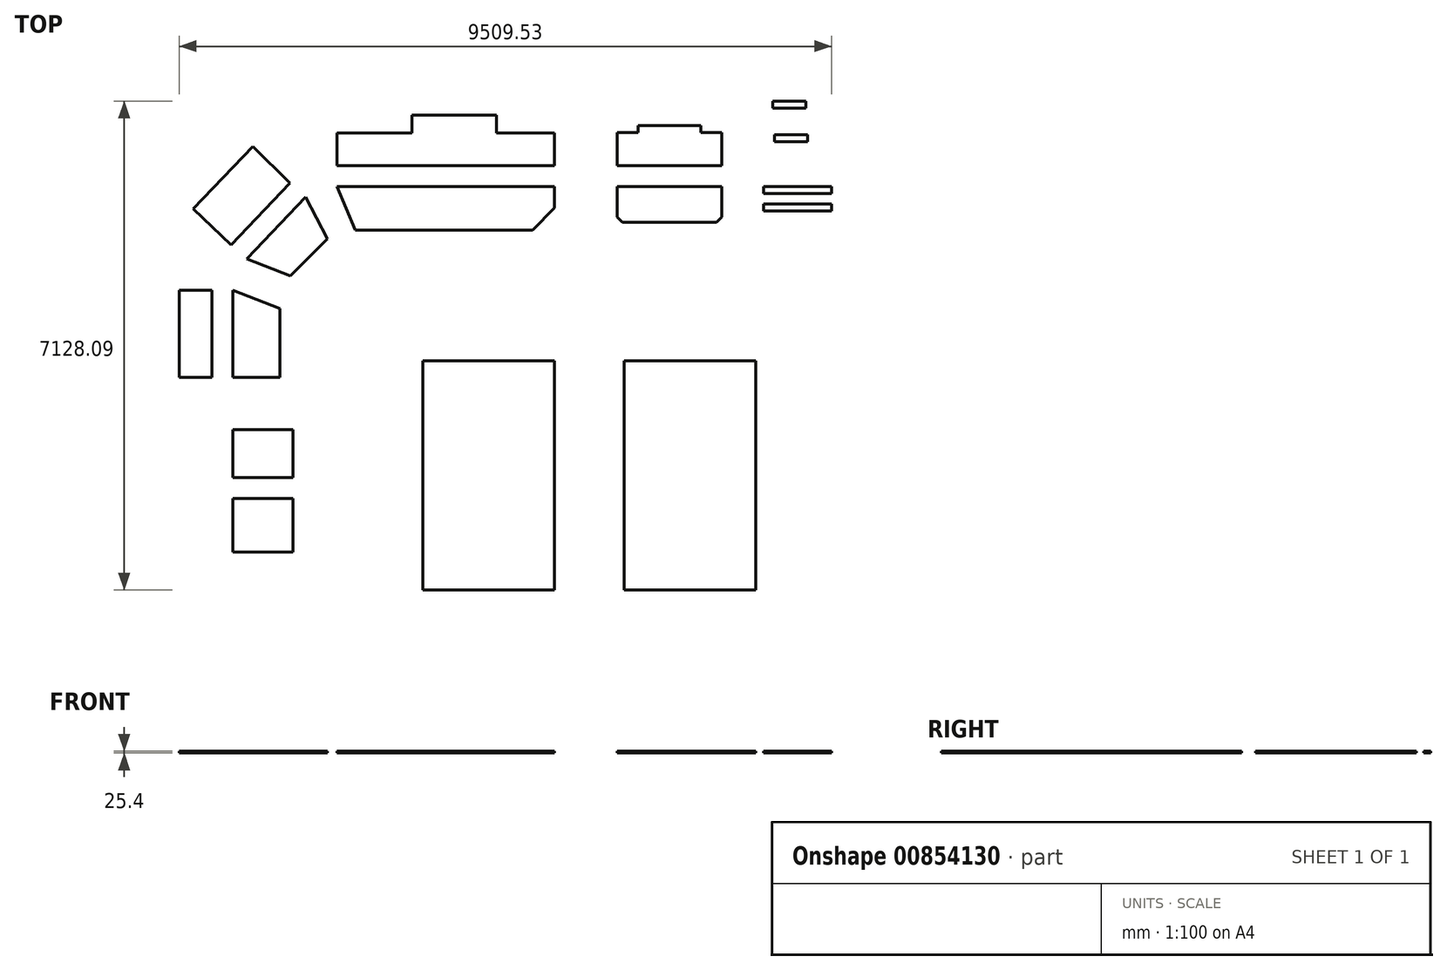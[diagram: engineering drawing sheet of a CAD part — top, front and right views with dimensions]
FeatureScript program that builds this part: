
annotation { "Feature Type Name" : "Feature", "Feature Type Description" : "" }
export const myFeature = defineFeature(function(context is Context, id is Id, definition is map)
    precondition{}
    {
        {
            var Q0;
            Q0=qCreatedBy(makeId("Top.planeOp"),FACE);
            var sketch = newSketch(context, id + "F0", { "sketchPlane" : qUnion([Q0])});
            skLineSegment(sketch, "E0", {"start": v(-3168.65, 0) * mm, "end": v(-2906.4, -633.1) * mm});
            skLineSegment(sketch, "E1", {"start": v(-2906.4, -633.1) * mm, "end": v(-321.96, -633.1) * mm});
            skLineSegment(sketch, "E2", {"start": v(-321.96, -633.1) * mm, "end": v(0, -311.15) * mm});
            skLineSegment(sketch, "E3", {"start": v(0, -311.15) * mm, "end": v(0, 0) * mm});
            skLineSegment(sketch, "E4", {"start": v(0, 0) * mm, "end": v(-3168.65, 0) * mm});
            skLineSegment(sketch, "E5", {"start": v(-3168.65, 781.05) * mm, "end": v(-3168.65, 304.8) * mm});
            skLineSegment(sketch, "E6", {"start": v(-3168.65, 304.8) * mm, "end": v(0, 304.8) * mm});
            skLineSegment(sketch, "E7", {"start": v(0, 304.8) * mm, "end": v(0, 781.05) * mm});
            skLineSegment(sketch, "E8", {"start": v(0, 781.05) * mm, "end": v(-847.73, 781.05) * mm});
            skLineSegment(sketch, "E9", {"start": v(-847.73, 781.05) * mm, "end": v(-847.73, 1041.4) * mm});
            skLineSegment(sketch, "E10", {"start": v(-847.73, 1041.4) * mm, "end": v(-2076.45, 1041.4) * mm});
            skLineSegment(sketch, "E11", {"start": v(-2076.45, 1041.4) * mm, "end": v(-2076.45, 781.05) * mm});
            skLineSegment(sketch, "E12", {"start": v(-2076.45, 781.05) * mm, "end": v(-3168.65, 781.05) * mm});
            skLineSegment(sketch, "E13", {"start": v(-3309.69, -760.97) * mm, "end": v(-3848.5, -1299.79) * mm});
            skLineSegment(sketch, "E14", {"start": v(-3848.5, -1299.79) * mm, "end": v(-4487.42, -1050.58) * mm});
            skLineSegment(sketch, "E15", {"start": v(-4487.42, -1050.58) * mm, "end": v(-3625.85, -152.4) * mm});
            skLineSegment(sketch, "E16", {"start": v(-3625.85, -152.4) * mm, "end": v(-3309.69, -760.97) * mm});
            skLineSegment(sketch, "E17", {"start": v(-3854.45, 49.2) * mm, "end": v(-4716.02, -848.97) * mm});
            skLineSegment(sketch, "E18", {"start": v(-4716.02, -848.97) * mm, "end": v(-5268.08, -323.81) * mm});
            skLineSegment(sketch, "E19", {"start": v(-5268.08, -323.81) * mm, "end": v(-4397.72, 583.53) * mm});
            skLineSegment(sketch, "E20", {"start": v(-4397.72, 583.53) * mm, "end": v(-3854.45, 49.2) * mm});
            skLineSegment(sketch, "E21", {"start": v(-4686.7, -1507.78) * mm, "end": v(-4000.9, -1774.48) * mm});
            skLineSegment(sketch, "E22", {"start": v(-4000.9, -1774.48) * mm, "end": v(-4000.9, -2777.78) * mm});
            skLineSegment(sketch, "E23", {"start": v(-4000.9, -2777.78) * mm, "end": v(-4686.7, -2777.78) * mm});
            skLineSegment(sketch, "E24", {"start": v(-4686.7, -2777.78) * mm, "end": v(-4686.7, -1507.78) * mm});
            skLineSegment(sketch, "E25.bottom", {"start": v(-5470.93, -1507.78) * mm, "end": v(-4991.5, -1507.78) * mm});
            skLineSegment(sketch, "E25.top", {"start": v(-5470.93, -2777.78) * mm, "end": v(-4991.5, -2777.78) * mm});
            skLineSegment(sketch, "E25.left", {"start": v(-5470.93, -1507.78) * mm, "end": v(-5470.93, -2777.78) * mm});
            skLineSegment(sketch, "E25.right", {"start": v(-4991.5, -1507.78) * mm, "end": v(-4991.5, -2777.78) * mm});
            skLineSegment(sketch, "E26", {"start": v(914.4, 787.4) * mm, "end": v(914.4, 304.8) * mm});
            skLineSegment(sketch, "E27", {"start": v(914.4, 304.8) * mm, "end": v(2438.4, 304.8) * mm});
            skLineSegment(sketch, "E28", {"start": v(2438.4, 304.8) * mm, "end": v(2438.4, 787.4) * mm});
            skLineSegment(sketch, "E29", {"start": v(2438.4, 787.4) * mm, "end": v(2133.6, 787.4) * mm});
            skLineSegment(sketch, "E30", {"start": v(2133.6, 787.4) * mm, "end": v(2133.6, 892.17) * mm});
            skLineSegment(sketch, "E31", {"start": v(2133.6, 892.17) * mm, "end": v(1219.2, 892.17) * mm});
            skLineSegment(sketch, "E32", {"start": v(1219.2, 892.17) * mm, "end": v(1219.2, 787.4) * mm});
            skLineSegment(sketch, "E33", {"start": v(1219.2, 787.4) * mm, "end": v(914.4, 787.4) * mm});
            skLineSegment(sketch, "E34", {"start": v(914.4, 0) * mm, "end": v(914.4, -444.5) * mm});
            skLineSegment(sketch, "E35", {"start": v(914.4, -444.5) * mm, "end": v(989.01, -519.11) * mm});
            skLineSegment(sketch, "E36", {"start": v(989.01, -519.11) * mm, "end": v(2363.79, -519.11) * mm});
            skLineSegment(sketch, "E37", {"start": v(2363.79, -519.11) * mm, "end": v(2438.4, -444.5) * mm});
            skLineSegment(sketch, "E38", {"start": v(2438.4, -444.5) * mm, "end": v(2438.4, 0) * mm});
            skLineSegment(sketch, "E39", {"start": v(2438.4, 0) * mm, "end": v(914.4, 0) * mm});
            skLineSegment(sketch, "E40.bottom", {"start": v(-4686.7, -3539.78) * mm, "end": v(-3810.4, -3539.78) * mm});
            skLineSegment(sketch, "E40.top", {"start": v(-4686.7, -4238.28) * mm, "end": v(-3810.4, -4238.28) * mm});
            skLineSegment(sketch, "E40.left", {"start": v(-4686.7, -3539.78) * mm, "end": v(-4686.7, -4238.28) * mm});
            skLineSegment(sketch, "E40.right", {"start": v(-3810.4, -3539.78) * mm, "end": v(-3810.4, -4238.28) * mm});
            skLineSegment(sketch, "E41.bottom", {"start": v(-4686.7, -4543.08) * mm, "end": v(-3810.4, -4543.08) * mm});
            skLineSegment(sketch, "E41.top", {"start": v(-4686.7, -5324.13) * mm, "end": v(-3810.4, -5324.13) * mm});
            skLineSegment(sketch, "E41.left", {"start": v(-4686.7, -4543.08) * mm, "end": v(-4686.7, -5324.13) * mm});
            skLineSegment(sketch, "E41.right", {"start": v(-3810.4, -4543.08) * mm, "end": v(-3810.4, -5324.13) * mm});
            skLineSegment(sketch, "E42.bottom", {"start": v(-1917.7, -2540) * mm, "end": v(0, -2540) * mm});
            skLineSegment(sketch, "E42.top", {"start": v(-1917.7, -5880.1) * mm, "end": v(0, -5880.1) * mm});
            skLineSegment(sketch, "E42.left", {"start": v(-1917.7, -2540) * mm, "end": v(-1917.7, -5880.1) * mm});
            skLineSegment(sketch, "E42.right", {"start": v(0, -2540) * mm, "end": v(0, -5880.1) * mm});
            skLineSegment(sketch, "E43.bottom", {"start": v(1016, -2540) * mm, "end": v(2933.7, -2540) * mm});
            skLineSegment(sketch, "E43.top", {"start": v(1016, -5880.1) * mm, "end": v(2933.7, -5880.1) * mm});
            skLineSegment(sketch, "E43.left", {"start": v(1016, -2540) * mm, "end": v(1016, -5880.1) * mm});
            skLineSegment(sketch, "E43.right", {"start": v(2933.7, -2540) * mm, "end": v(2933.7, -5880.1) * mm});
            skLineSegment(sketch, "E44.bottom", {"start": v(3048, -254) * mm, "end": v(4038.6, -254) * mm});
            skLineSegment(sketch, "E44.top", {"start": v(3048, -355.6) * mm, "end": v(4038.6, -355.6) * mm});
            skLineSegment(sketch, "E44.left", {"start": v(3048, -254) * mm, "end": v(3048, -355.6) * mm});
            skLineSegment(sketch, "E44.right", {"start": v(4038.6, -254) * mm, "end": v(4038.6, -355.6) * mm});
            skLineSegment(sketch, "E45.bottom", {"start": v(3048, 0) * mm, "end": v(4038.6, 0) * mm});
            skLineSegment(sketch, "E45.top", {"start": v(3048, -101.6) * mm, "end": v(4038.6, -101.6) * mm});
            skLineSegment(sketch, "E45.left", {"start": v(3048, 0) * mm, "end": v(3048, -101.6) * mm});
            skLineSegment(sketch, "E45.right", {"start": v(4038.6, 0) * mm, "end": v(4038.6, -101.6) * mm});
            skLineSegment(sketch, "E46.bottom", {"start": v(3205.8, 754.8) * mm, "end": v(3688.4, 754.8) * mm});
            skLineSegment(sketch, "E46.top", {"start": v(3205.8, 653.2) * mm, "end": v(3688.4, 653.2) * mm});
            skLineSegment(sketch, "E46.left", {"start": v(3205.8, 754.8) * mm, "end": v(3205.8, 653.2) * mm});
            skLineSegment(sketch, "E46.right", {"start": v(3688.4, 754.8) * mm, "end": v(3688.4, 653.2) * mm});
            skLineSegment(sketch, "E47.bottom", {"start": v(3181.45, 1247.99) * mm, "end": v(3664.05, 1247.99) * mm});
            skLineSegment(sketch, "E47.top", {"start": v(3181.45, 1146.39) * mm, "end": v(3664.05, 1146.39) * mm});
            skLineSegment(sketch, "E47.left", {"start": v(3181.45, 1247.99) * mm, "end": v(3181.45, 1146.39) * mm});
            skLineSegment(sketch, "E47.right", {"start": v(3664.05, 1247.99) * mm, "end": v(3664.05, 1146.39) * mm});
            skSolve(sketch);
        }
        {
            var Q0;
            Q0=makeQuery(id+"F0.imprint","IMPRINT",FACE,{"disambiguationData":[TD([[makeQuery(id+"F0.imprint","IMPRINT",EDGE,{"derivedFrom":sQuery(id+"F0.wireOp",EDGE,"E13")}),-1.0]])]});
            var Q1;
            Q1=makeQuery(id+"F0.imprint","IMPRINT",FACE,{"disambiguationData":[TD([[makeQuery(id+"F0.imprint","IMPRINT",EDGE,{"derivedFrom":sQuery(id+"F0.wireOp",EDGE,"E0")}),1.0]])]});
            var Q2;
            Q2=makeQuery(id+"F0.imprint","IMPRINT",FACE,{"disambiguationData":[TD([[makeQuery(id+"F0.imprint","IMPRINT",EDGE,{"derivedFrom":sQuery(id+"F0.wireOp",EDGE,"E5")}),1.0]])]});
            var Q3;
            Q3=makeQuery(id+"F0.imprint","IMPRINT",FACE,{"disambiguationData":[TD([[makeQuery(id+"F0.imprint","IMPRINT",EDGE,{"derivedFrom":sQuery(id+"F0.wireOp",EDGE,"E21")}),-1.0]])]});
            var Q4;
            Q4=makeQuery(id+"F0.imprint","IMPRINT",FACE,{"disambiguationData":[TD([[makeQuery(id+"F0.imprint","IMPRINT",EDGE,{"derivedFrom":sQuery(id+"F0.wireOp",EDGE,"E40.bottom")}),-1.0]])]});
            var Q5;
            Q5=makeQuery(id+"F0.imprint","IMPRINT",FACE,{"disambiguationData":[TD([[makeQuery(id+"F0.imprint","IMPRINT",EDGE,{"derivedFrom":sQuery(id+"F0.wireOp",EDGE,"E41.bottom")}),-1.0]])]});
            var Q6;
            Q6=makeQuery(id+"F0.imprint","IMPRINT",FACE,{"disambiguationData":[TD([[makeQuery(id+"F0.imprint","IMPRINT",EDGE,{"derivedFrom":sQuery(id+"F0.wireOp",EDGE,"E42.bottom")}),-1.0]])]});
            var Q7;
            Q7=makeQuery(id+"F0.imprint","IMPRINT",FACE,{"disambiguationData":[TD([[makeQuery(id+"F0.imprint","IMPRINT",EDGE,{"derivedFrom":sQuery(id+"F0.wireOp",EDGE,"E43.bottom")}),-1.0]])]});
            var Q8;
            Q8=makeQuery(id+"F0.imprint","IMPRINT",FACE,{"disambiguationData":[TD([[makeQuery(id+"F0.imprint","IMPRINT",EDGE,{"derivedFrom":sQuery(id+"F0.wireOp",EDGE,"E25.bottom")}),-1.0]])]});
            var Q9;
            Q9=makeQuery(id+"F0.imprint","IMPRINT",FACE,{"disambiguationData":[TD([[makeQuery(id+"F0.imprint","IMPRINT",EDGE,{"derivedFrom":sQuery(id+"F0.wireOp",EDGE,"E26")}),1.0]])]});
            var Q10;
            Q10=makeQuery(id+"F0.imprint","IMPRINT",FACE,{"disambiguationData":[TD([[makeQuery(id+"F0.imprint","IMPRINT",EDGE,{"derivedFrom":sQuery(id+"F0.wireOp",EDGE,"E34")}),1.0]])]});
            var Q11;
            Q11=makeQuery(id+"F0.imprint","IMPRINT",FACE,{"disambiguationData":[TD([[makeQuery(id+"F0.imprint","IMPRINT",EDGE,{"derivedFrom":sQuery(id+"F0.wireOp",EDGE,"E17")}),-1.0]])]});
            var Q12;
            Q12=makeQuery(id+"F0.imprint","IMPRINT",FACE,{"disambiguationData":[TD([[makeQuery(id+"F0.imprint","IMPRINT",EDGE,{"derivedFrom":sQuery(id+"F0.wireOp",EDGE,"E45.bottom")}),-1.0]])]});
            var Q13;
            Q13=makeQuery(id+"F0.imprint","IMPRINT",FACE,{"disambiguationData":[TD([[makeQuery(id+"F0.imprint","IMPRINT",EDGE,{"derivedFrom":sQuery(id+"F0.wireOp",EDGE,"E44.bottom")}),-1.0]])]});
            var Q14;
            Q14=makeQuery(id+"F0.imprint","IMPRINT",FACE,{"disambiguationData":[TD([[makeQuery(id+"F0.imprint","IMPRINT",EDGE,{"derivedFrom":sQuery(id+"F0.wireOp",EDGE,"E47.bottom")}),-1.0]])]});
            var Q15;
            Q15=makeQuery(id+"F0.imprint","IMPRINT",FACE,{"disambiguationData":[TD([[makeQuery(id+"F0.imprint","IMPRINT",EDGE,{"derivedFrom":sQuery(id+"F0.wireOp",EDGE,"E46.bottom")}),-1.0]])]});
            extrude(context, id + "F1", {"entities" : qUnion([Q0, Q1, Q2, Q3, Q4, Q5, Q6, Q7, Q8, Q9, Q10, Q11, Q12, Q13, Q14, Q15]), "depth" : 25.4 * mm, "offsetDistance" : 25.4 * mm});
        }
    });
